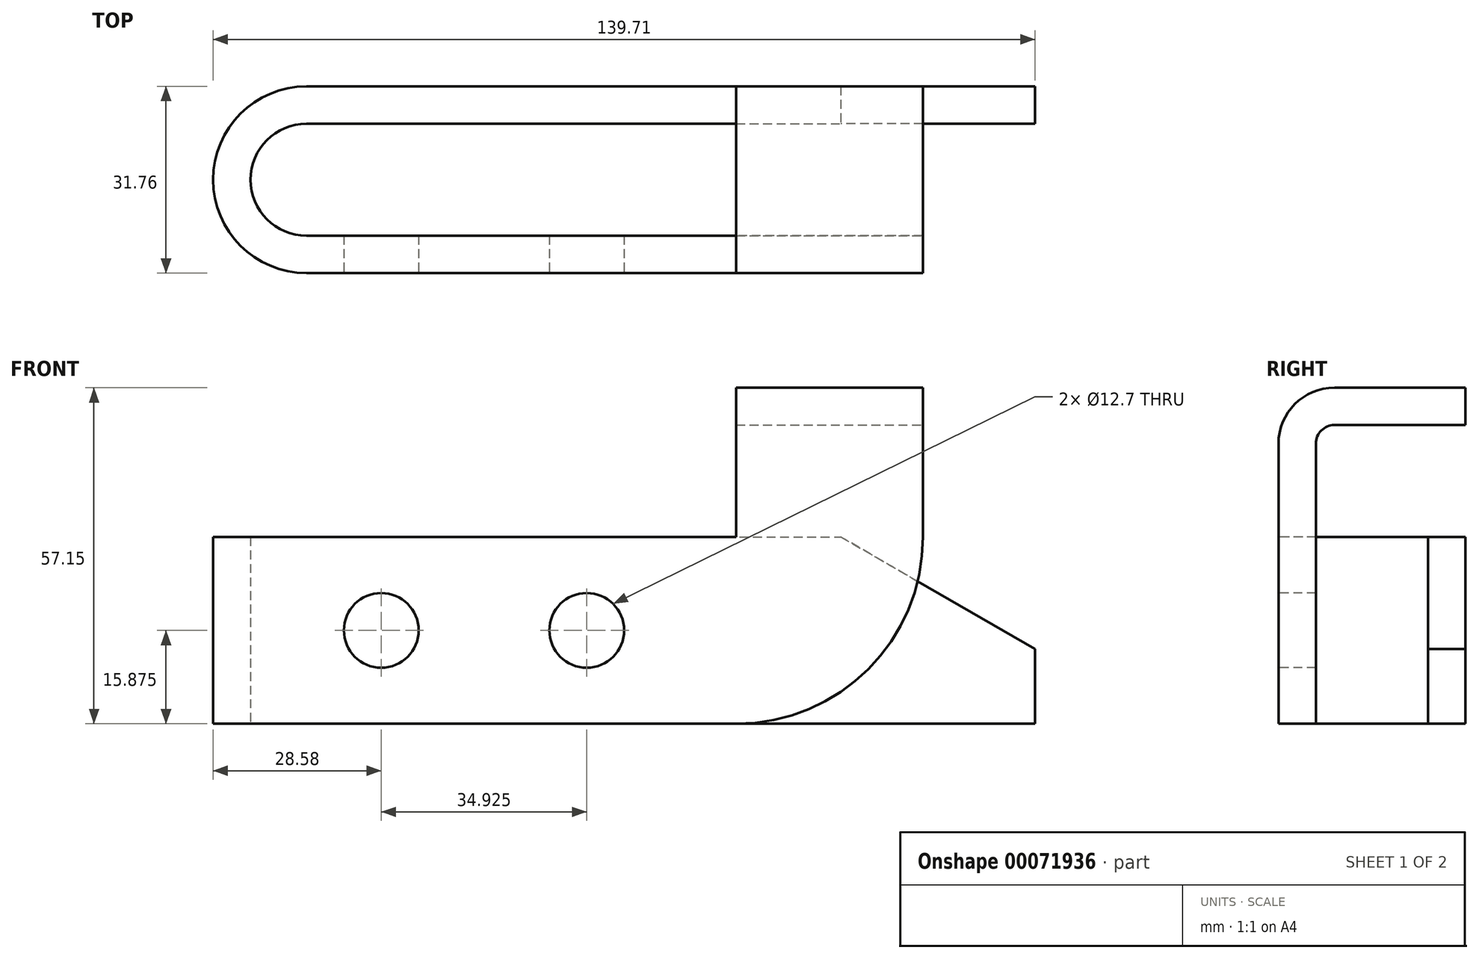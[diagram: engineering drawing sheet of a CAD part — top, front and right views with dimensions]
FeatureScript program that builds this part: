
annotation { "Feature Type Name" : "Feature", "Feature Type Description" : "" }
export const myFeature = defineFeature(function(context is Context, id is Id, definition is map)
    precondition{}
    {
        {
            var Q0;
            Q0=qCreatedBy(makeId("Top.planeOp"),FACE);
            var sketch = newSketch(context, id + "F0", { "sketchPlane" : qUnion([Q0])});
            skArc(sketch, "E0", {"start": v(0, 15.88) * mm, "mid": v(-15.88, 0) * mm, "end": v(0, -15.88) * mm});
            skArc(sketch, "E1.0", {"start": v(0, 9.52) * mm, "mid": v(-9.52, 0) * mm, "end": v(0, -9.52) * mm});
            skLineSegment(sketch, "E2", {"start": v(0, -15.88) * mm, "end": v(104.78, -15.88) * mm});
            skLineSegment(sketch, "E3", {"start": v(0, 0) * mm, "end": v(124.83, 0) * mm, "construction": true});
            skLineSegment(sketch, "E4.MirrorCS", {"start": v(0, 15.88) * mm, "end": v(123.83, 15.88) * mm});
            skLineSegment(sketch, "E5", {"start": v(123.83, 15.88) * mm, "end": v(123.83, 9.52) * mm});
            skLineSegment(sketch, "E6.0", {"start": v(0, 9.52) * mm, "end": v(123.83, 9.52) * mm});
            skLineSegment(sketch, "E7.0", {"start": v(0, -9.52) * mm, "end": v(104.78, -9.52) * mm});
            skPoint(sketch, "E8.orphan", {"position": v(104.78, 15.88) * mm});
            skLineSegment(sketch, "E9", {"start": v(104.78, -9.52) * mm, "end": v(104.78, -15.88) * mm});
            skSolve(sketch);
        }
        {
            var Q0;
            Q0=makeQuery(id+"F0.imprint","IMPRINT",FACE,{"disambiguationData":[TD([[makeQuery(id+"F0.imprint","IMPRINT",EDGE,{"derivedFrom":sQuery(id+"F0.wireOp",EDGE,"E0")}),1.0]])]});
            extrude(context, id + "F1", {"entities" : qUnion([Q0]), "depth" : 31.75 * mm});
        }
        {
            var Q0;
            Q0=makeQuery(id+"F1.opExtrude","SWEPT_FACE",FACE,{"disambiguationData":[OSD([sQuery(id+"F0.wireOp",EDGE,"E6.0")])]});
            var sketch = newSketch(context, id + "F2", { "sketchPlane" : qUnion([Q0])});
            skLineSegment(sketch, "E10.0", {"start": v(0, 31.75) * mm, "end": v(123.83, 31.75) * mm});
            skLineSegment(sketch, "E11.0", {"start": v(123.83, 31.75) * mm, "end": v(123.83, 12.7) * mm});
            skLineSegment(sketch, "E12", {"start": v(123.83, 12.7) * mm, "end": v(90.83, 31.75) * mm});
            skPoint(sketch, "E13.orphan", {"position": v(123.83, 0) * mm});
            skSolve(sketch);
        }
        {
            var Q0;
            {var subQ0=sQuery(id+"F2.wireOp",EDGE,"E11.0");Q0=makeQuery(id+"F2.imprint","IMPRINT",FACE,{"disambiguationData":[TD([[makeQuery(id+"F2.imprint","IMPRINT",EDGE,{"derivedFrom":subQ0}),-1.0]])]});}
            extrude(context, id + "F3", {"entities" : qUnion([Q0]), "operationType" : NewBodyOperationType.REMOVE, "oppositeDirection" : true, "depth" : 25.4 * mm});
        }
        {
            var Q0;
            Q0=makeQuery(id+"F1.opExtrude","SWEPT_FACE",FACE,{"disambiguationData":[OSD([sQuery(id+"F0.wireOp",EDGE,"E9")])]});
            var sketch = newSketch(context, id + "F4", { "sketchPlane" : qUnion([Q0])});
            skLineSegment(sketch, "E14.0", {"start": v(-15.88, 50.8) * mm, "end": v(-15.88, 31.75) * mm});
            skLineSegment(sketch, "E15.0", {"start": v(-9.52, 50.8) * mm, "end": v(-9.52, 31.75) * mm});
            skLineSegment(sketch, "E16.bottom", {"start": v(-15.88, 57.15) * mm, "end": v(15.88, 57.15) * mm});
            skLineSegment(sketch, "E16.top", {"start": v(-9.52, 50.8) * mm, "end": v(15.88, 50.8) * mm});
            skLineSegment(sketch, "E16.left", {"start": v(-15.88, 57.15) * mm, "end": v(-15.88, 50.8) * mm});
            skLineSegment(sketch, "E16.right", {"start": v(15.88, 57.15) * mm, "end": v(15.88, 50.8) * mm});
            skPoint(sketch, "E17.0.end.orphan", {"position": v(-15.88, 31.75) * mm});
            skPoint(sketch, "E17.0.start.orphan", {"position": v(-9.52, 31.75) * mm});
            skLineSegment(sketch, "E18", {"start": v(-15.88, 31.75) * mm, "end": v(-9.52, 31.75) * mm});
            skPoint(sketch, "E19.orphan", {"position": v(-15.88, 0) * mm});
            skPoint(sketch, "E20.orphan", {"position": v(-9.52, 0) * mm});
            skSolve(sketch);
        }
        {
            var Q0;
            Q0=makeQuery(id+"F4.imprint","IMPRINT",FACE,{"disambiguationData":[TD([[makeQuery(id+"F4.imprint","IMPRINT",EDGE,{"derivedFrom":sQuery(id+"F4.wireOp",EDGE,"E14.0")}),1.0]])]});
            extrude(context, id + "F5", {"entities" : qUnion([Q0]), "oppositeDirection" : true, "depth" : 31.75 * mm});
        }
        {
            var Q0;
            Q0=makeQuery(id+"F1.opExtrude","SWEPT_BODY",BODY,{"disambiguationData":[OSD([sQuery(id+"F0.wireOp",EDGE,"E0"),sQuery(id+"F0.wireOp",EDGE,"E1.0"),sQuery(id+"F0.wireOp",EDGE,"E2"),sQuery(id+"F0.wireOp",EDGE,"E4.MirrorCS"),sQuery(id+"F0.wireOp",EDGE,"E5"),sQuery(id+"F0.wireOp",EDGE,"E6.0"),sQuery(id+"F0.wireOp",EDGE,"E7.0"),sQuery(id+"F0.wireOp",EDGE,"E9")])]});
            var Q1;
            Q1=makeQuery(id+"F5.opExtrude","SWEPT_BODY",BODY,{"disambiguationData":[OSD([sQuery(id+"F4.wireOp",EDGE,"E14.0"),sQuery(id+"F4.wireOp",EDGE,"E15.0"),sQuery(id+"F4.wireOp",EDGE,"E16.bottom"),sQuery(id+"F4.wireOp",EDGE,"E16.top"),sQuery(id+"F4.wireOp",EDGE,"E16.left"),sQuery(id+"F4.wireOp",EDGE,"E16.right"),sQuery(id+"F4.wireOp",EDGE,"E18")])]});
            booleanBodies(context, id + "F6", {"operationType" : BooleanOperationType.UNION, "tools" : qUnion([Q0, Q1])});
        }
        {
            var Q0;
            Q0=makeQuery(id+"F1.opExtrude","CAP_EDGE",EDGE,{"disambiguationData":[OSD([sQuery(id+"F0.wireOp",EDGE,"E9")])],"isStart":true});
            fillet(context, id + "F7", {"entities" : qUnion([Q0]), "radius" : 31.75 * mm, "tangentPropagation" : true, "allowEdgeOverflow" : false});
        }
        {
            var Q0;
            Q0=makeQuery(id+"F5.opExtrude","SWEPT_EDGE",EDGE,{"disambiguationData":[OSD([sQuery(id+"F4.wireOp",EDGE,"E16.bottom"),sQuery(id+"F4.wireOp",EDGE,"E16.left")])]});
            fillet(context, id + "F8", {"entities" : qUnion([Q0]), "radius" : 9.52 * mm, "tangentPropagation" : true, "allowEdgeOverflow" : false});
        }
        {
            var Q0;
            Q0=makeQuery(id+"F5.opExtrude","SWEPT_EDGE",EDGE,{"disambiguationData":[OSD([sQuery(id+"F4.wireOp",EDGE,"E15.0"),sQuery(id+"F4.wireOp",EDGE,"E16.top")])]});
            fillet(context, id + "F9", {"entities" : qUnion([Q0]), "radius" : 3.17 * mm, "tangentPropagation" : true, "allowEdgeOverflow" : false});
        }
        {
            var Q0;
            Q0=makeQuery(id+"F6.opBoolean","MERGE",FACE,{"derivedFrom":[makeQuery(id+"F1.opExtrude","SWEPT_FACE",FACE,{"disambiguationData":[OSD([sQuery(id+"F0.wireOp",EDGE,"E2")])]}),makeQuery(id+"F5.opExtrude","SWEPT_FACE",FACE,{"disambiguationData":[OSD([sQuery(id+"F4.wireOp",EDGE,"E14.0"),sQuery(id+"F4.wireOp",EDGE,"E16.left")])]})]});
            var sketch = newSketch(context, id + "F10", { "sketchPlane" : qUnion([Q0])});
            skCircle(sketch, "E21", {"center": v(12.7, 15.88) * mm, "radius": 6.35 * mm});
            skCircle(sketch, "E22", {"center": v(47.62, 15.88) * mm, "radius": 6.35 * mm});
            skSolve(sketch);
        }
        {
            var Q0;
            Q0=makeQuery(id+"F10.imprint","IMPRINT",FACE,{"disambiguationData":[TD([[makeQuery(id+"F10.imprint","IMPRINT",EDGE,{"derivedFrom":sQuery(id+"F10.wireOp",EDGE,"E21")}),1.0]])]});
            var Q1;
            Q1=makeQuery(id+"F10.imprint","IMPRINT",FACE,{"disambiguationData":[TD([[makeQuery(id+"F10.imprint","IMPRINT",EDGE,{"derivedFrom":sQuery(id+"F10.wireOp",EDGE,"E22")}),1.0]])]});
            extrude(context, id + "F11", {"entities" : qUnion([Q0, Q1]), "operationType" : NewBodyOperationType.REMOVE, "oppositeDirection" : true, "depth" : 6.35 * mm});
        }
    });
